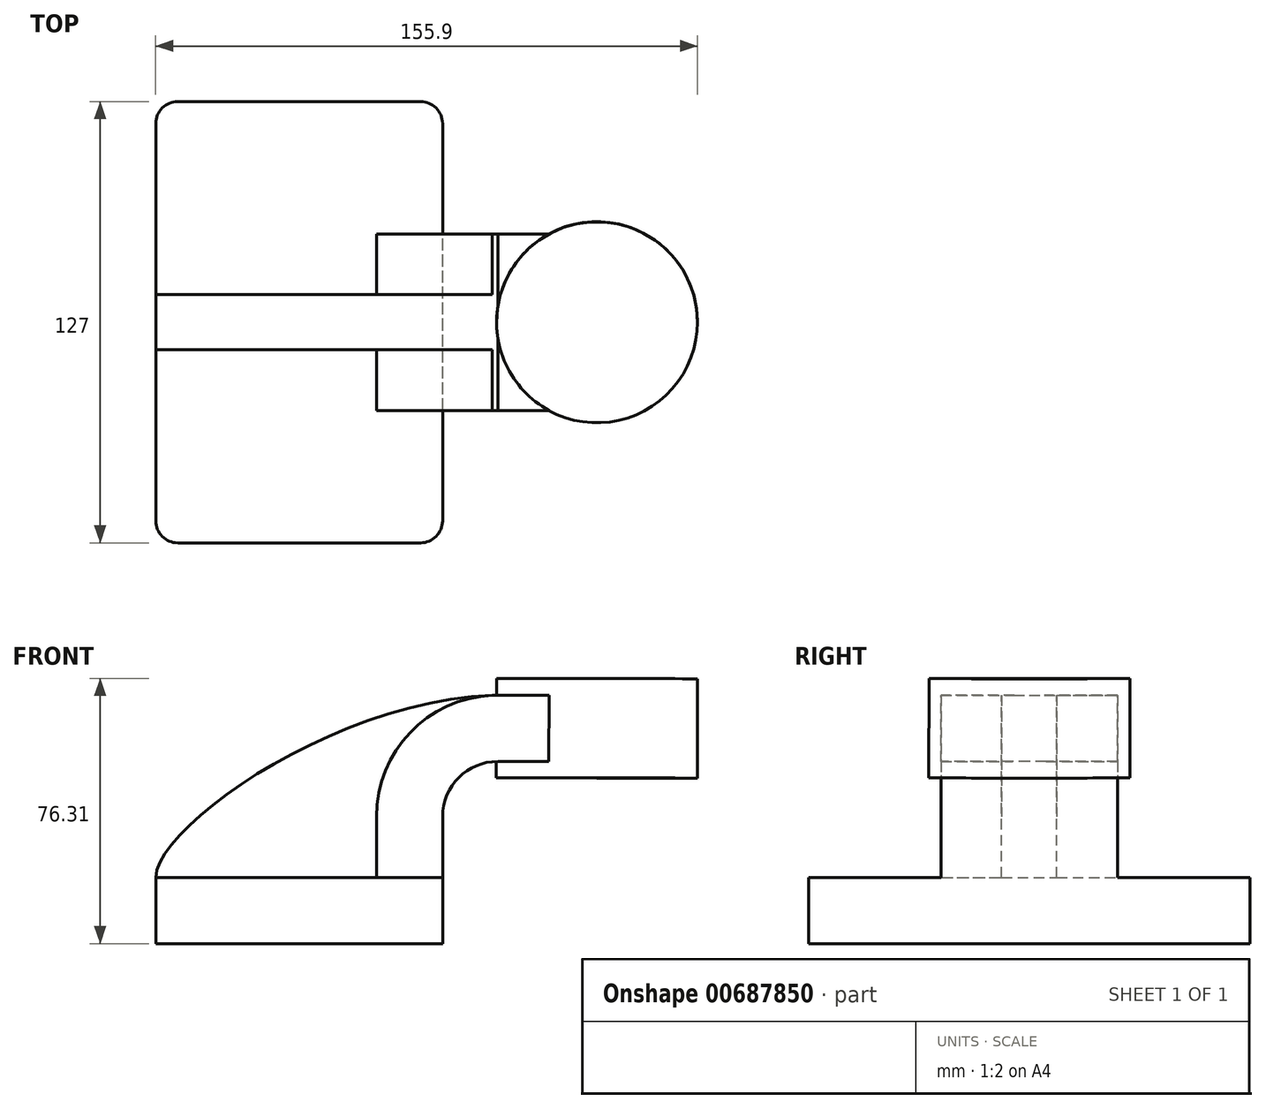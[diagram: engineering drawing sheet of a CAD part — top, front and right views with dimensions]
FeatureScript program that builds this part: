
annotation { "Feature Type Name" : "Feature", "Feature Type Description" : "" }
export const myFeature = defineFeature(function(context is Context, id is Id, definition is map)
    precondition{}
    {
        {
            var Q0;
            Q0=qCreatedBy(makeId("Front.planeOp"),FACE);
            var sketch = newSketch(context, id + "F0", { "sketchPlane" : qUnion([Q0])});
            skLineSegment(sketch, "E0.bottom", {"start": v(-41.28, 9.52) * mm, "end": v(41.28, 9.53) * mm});
            skLineSegment(sketch, "E0.top", {"start": v(-41.28, -9.53) * mm, "end": v(41.28, -9.53) * mm});
            skLineSegment(sketch, "E0.left", {"start": v(-41.28, 9.52) * mm, "end": v(-41.28, -9.53) * mm});
            skLineSegment(sketch, "E0.right", {"start": v(41.28, 9.53) * mm, "end": v(41.28, -9.52) * mm});
            skPoint(sketch, "E0.middle", {"position": v(0, 0) * mm});
            skLineSegment(sketch, "E1.bottom", {"start": v(63.82, 66.67) * mm, "end": v(114.62, 66.67) * mm});
            skLineSegment(sketch, "E1.top", {"start": v(63.82, 38.1) * mm, "end": v(114.62, 38.1) * mm});
            skLineSegment(sketch, "E1.left", {"start": v(63.82, 66.67) * mm, "end": v(63.82, 38.1) * mm});
            skLineSegment(sketch, "E1.right", {"start": v(114.62, 66.67) * mm, "end": v(114.62, 38.1) * mm});
            skLineSegment(sketch, "E2", {"start": v(41.27, 9.53) * mm, "end": v(41.27, 27) * mm});
            skArc(sketch, "E3", {"start": v(41.27, 27) * mm, "mid": v(45.92, 38.23) * mm, "end": v(57.15, 42.88) * mm});
            skLineSegment(sketch, "E4", {"start": v(57.15, 42.88) * mm, "end": v(85.72, 42.88) * mm});
            skLineSegment(sketch, "E5.0", {"start": v(57.15, 61.93) * mm, "end": v(85.72, 61.93) * mm});
            skArc(sketch, "E5.1", {"start": v(22.22, 27) * mm, "mid": v(32.45, 51.7) * mm, "end": v(57.15, 61.93) * mm});
            skLineSegment(sketch, "E5.2", {"start": v(22.22, 9.53) * mm, "end": v(22.22, 27) * mm});
            skLineSegment(sketch, "E6", {"start": v(85.67, 38.1) * mm, "end": v(85.72, 66.67) * mm});
            skFitSpline(sketch, "E7", {"points": [v(-41.28, 9.52) * mm, v(57.15, 61.93) * mm], "startDerivative": vector(1.26, 44.8) * mm, "endDerivative": vector(137.5, 1.86) * mm});
            skSolve(sketch);
        }
        {
            var Q0;
            Q0=makeQuery(id+"F0.imprint","IMPRINT",FACE,{"disambiguationData":[TD([[makeQuery(id+"F0.imprint","IMPRINT",EDGE,{"derivedFrom":sQuery(id+"F0.wireOp",EDGE,"E0.top")}),1.0]])]});
            extrude(context, id + "F1", {"entities" : qUnion([Q0]), "endBound" : BoundingType.SYMMETRIC, "depth" : 127 * mm, "offsetDistance" : 25.4 * mm});
        }
        {
            var Q0;
            {var subQ1=sQuery(id+"F0.wireOp",EDGE,"E2");Q0=makeQuery(id+"F0.imprint","IMPRINT",FACE,{"disambiguationData":[TD([[makeQuery(id+"F0.imprint","IMPRINT",EDGE,{"derivedFrom":subQ1}),1.0]])]});}
            var Q1;
            {var subQ0=sQuery(id+"F0.wireOp",EDGE,"E5.0");var subQ1=sQuery(id+"F0.wireOp",EDGE,"E1.left");var subQ2=makeQuery(id+"F0.imprint","INTERSECT",VERTEX,{"derivedFrom":[subQ1,subQ0]});Q1=makeQuery(id+"F0.imprint","IMPRINT",FACE,{"disambiguationData":[TD([[makeQuery(id+"F0.imprint","IMPRINT",EDGE,{"disambiguationData":[TD([[subQ2,-1.0]])],"derivedFrom":subQ1}),1.0]])]});}
            extrude(context, id + "F2", {"entities" : qUnion([Q0, Q1]), "operationType" : NewBodyOperationType.ADD, "endBound" : BoundingType.SYMMETRIC, "depth" : 50.8 * mm, "offsetDistance" : 25.4 * mm});
        }
        {
            var Q0;
            {var subQ3=sQuery(id+"F0.wireOp",EDGE,"E5.2");Q0=makeQuery(id+"F0.imprint","IMPRINT",FACE,{"disambiguationData":[TD([[makeQuery(id+"F0.imprint","IMPRINT",EDGE,{"derivedFrom":subQ3}),1.0]])]});}
            extrude(context, id + "F3", {"entities" : qUnion([Q0]), "operationType" : NewBodyOperationType.ADD, "endBound" : BoundingType.SYMMETRIC, "depth" : 15.88 * mm, "offsetDistance" : 25.4 * mm});
        }
        {
            var Q0;
            {var subQ4=sQuery(id+"F0.wireOp",EDGE,"E1.right");Q0=makeQuery(id+"F0.imprint","IMPRINT",FACE,{"disambiguationData":[TD([[makeQuery(id+"F0.imprint","IMPRINT",EDGE,{"derivedFrom":subQ4}),-1.0]])]});}
            var Q1;
            Q1=sQuery(id+"F0.wireOp",EDGE,"E6");
            revolve(context, id + "F4", {"operationType" : NewBodyOperationType.ADD, "entities" : qUnion([Q0]), "axis" : qUnion([Q1]), "revolveType" : RevolveType.FULL});
        }
        {
            var Q0;
            Q0=makeQuery(id+"F1.opExtrude","CAP_EDGE",EDGE,{"disambiguationData":[OSD([sQuery(id+"F0.wireOp",EDGE,"E0.left")])],"isStart":false});
            var Q1;
            Q1=makeQuery(id+"F1.opExtrude","CAP_EDGE",EDGE,{"disambiguationData":[OSD([sQuery(id+"F0.wireOp",EDGE,"E0.right")])],"isStart":false});
            var Q2;
            Q2=makeQuery(id+"F1.opExtrude","CAP_EDGE",EDGE,{"disambiguationData":[OSD([sQuery(id+"F0.wireOp",EDGE,"E0.left")])],"isStart":true});
            var Q3;
            Q3=makeQuery(id+"F1.opExtrude","CAP_EDGE",EDGE,{"disambiguationData":[OSD([sQuery(id+"F0.wireOp",EDGE,"E0.right")])],"isStart":true});
            fillet(context, id + "F5", {"entities" : qUnion([Q0, Q1, Q2, Q3]), "radius" : 6.35 * mm, "tangentPropagation" : true, "allowEdgeOverflow" : false});
        }
    });
